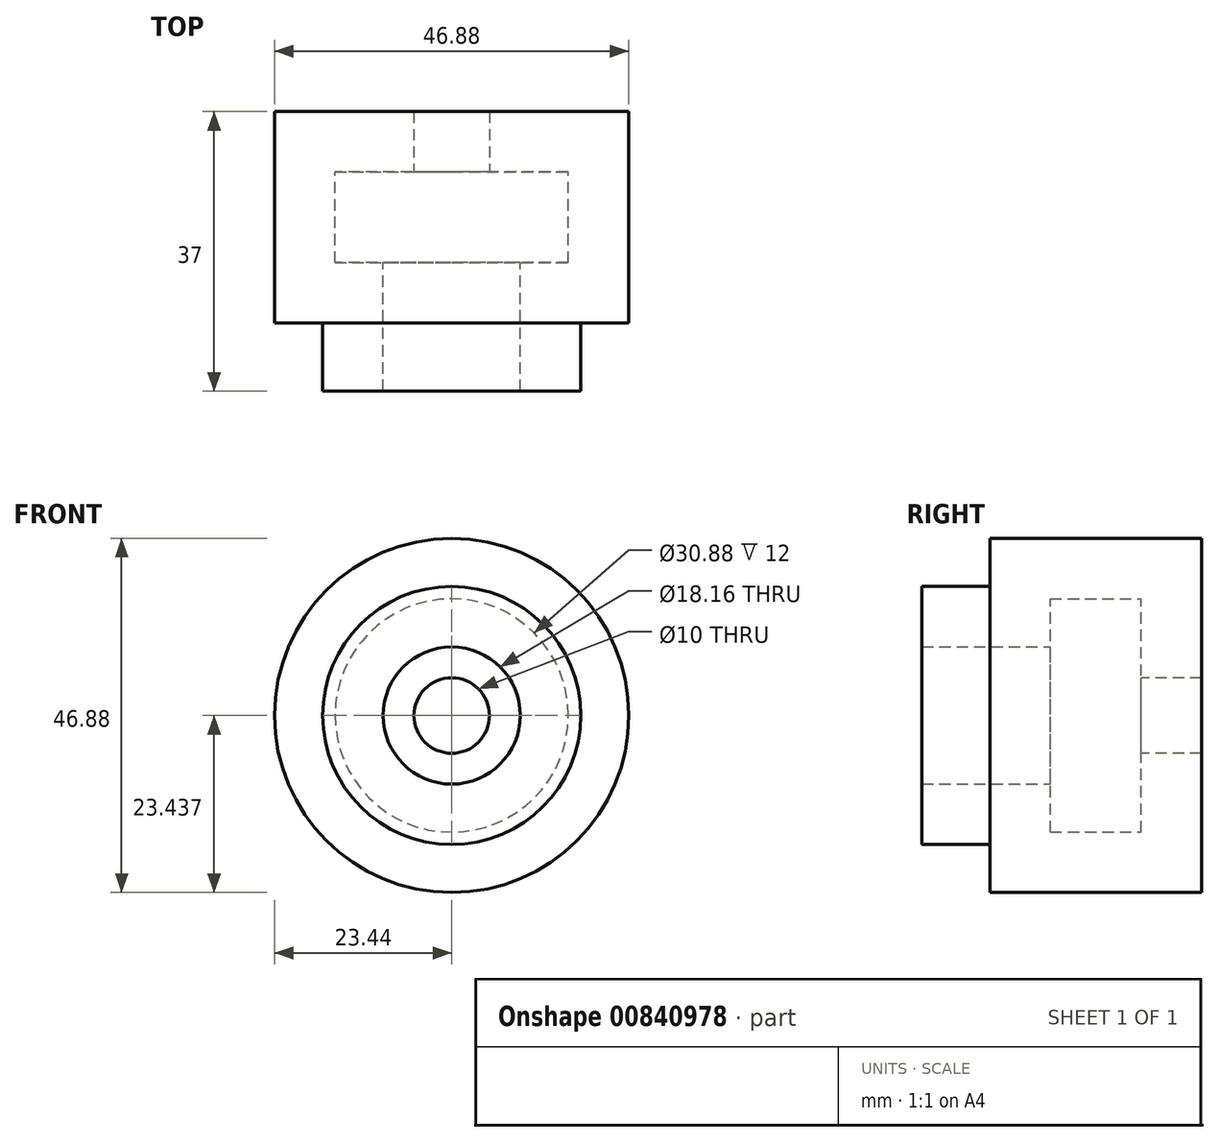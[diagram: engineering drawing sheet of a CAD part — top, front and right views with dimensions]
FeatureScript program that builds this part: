
annotation { "Feature Type Name" : "Feature", "Feature Type Description" : "" }
export const myFeature = defineFeature(function(context is Context, id is Id, definition is map)
    precondition{}
    {
        {
            var Q0;
            Q0=qCreatedBy(makeId("Front.planeOp"),FACE);
            var sketch = newSketch(context, id + "F0", { "sketchPlane" : qUnion([Q0])});
            skCircle(sketch, "E0", {"center": v(0, 23.7) * mm, "radius": 23.44 * mm});
            skSolve(sketch);
        }
        {
            var Q0;
            Q0=makeQuery(id+"F0.imprint","IMPRINT",FACE,{"disambiguationData":[TD([[makeQuery(id+"F0.imprint","IMPRINT",EDGE,{"derivedFrom":sQuery(id+"F0.wireOp",EDGE,"E0")}),1.0]])]});
            var Q1;
            Q1=sQuery(id+"F0.wireOp",EDGE,"E0");
            extrude(context, id + "F1", {"entities" : qUnion([Q0]), "surfaceEntities" : qUnion([Q1]), "depth" : 28 * mm, "offsetDistance" : 25.4 * mm});
        }
        {
            var Q0;
            Q0=makeQuery(id+"F1.opExtrude","SWEPT_BODY",BODY,{"disambiguationData":[OSD([sQuery(id+"F0.wireOp",EDGE,"E0")])]});
            transform(context, id + "F2", {"entities" : qUnion([Q0]), "transformType" : TransformType.TRANSLATION_3D, "dx" : 0 * mm, "dy" : 25.65 * mm, "dz" : 0 * mm, "makeCopy" : false});
        }
        {
            var Q0;
            Q0=makeQuery(id+"F1.opExtrude","CAP_FACE",FACE,{"disambiguationData":[OSD([sQuery(id+"F0.wireOp",EDGE,"E0")])],"isStart":false});
            var sketch = newSketch(context, id + "F3", { "sketchPlane" : qUnion([Q0])});
            skCircle(sketch, "E1", {"center": v(0, 23.7) * mm, "radius": 17.08 * mm});
            skSolve(sketch);
        }
        {
            var Q0;
            Q0=makeQuery(id+"F3.imprint","IMPRINT",FACE,{"disambiguationData":[TD([[makeQuery(id+"F3.imprint","IMPRINT",EDGE,{"derivedFrom":sQuery(id+"F3.wireOp",EDGE,"E1")}),1.0]])]});
            extrude(context, id + "F4", {"entities" : qUnion([Q0]), "operationType" : NewBodyOperationType.ADD, "surfaceOperationType" : NewSurfaceOperationType.ADD, "depth" : 9 * mm, "offsetDistance" : 25 * mm});
        }
        {
            var Q0;
            Q0=makeQuery(id+"F4.opExtrude","CAP_FACE",FACE,{"disambiguationData":[OSD([sQuery(id+"F3.wireOp",EDGE,"E1")])],"isStart":false});
            var Q1;
            Q1=makeQuery(id+"F1.opExtrude","SWEPT_BODY",BODY,{"disambiguationData":[OSD([sQuery(id+"F0.wireOp",EDGE,"E0")])]});
            shell(context, id + "F5", {"entities" : qUnion([Q0]), "parts" : qUnion([Q1]), "thickness" : 8 * mm});
        }
        {
            var Q0;
            Q0=sQuery(id+"F0.wireOp",VERTEX,"E0.center");
            var Q1;
            Q1=makeQuery(id+"F1.opExtrude","SWEPT_BODY",BODY,{"disambiguationData":[OSD([sQuery(id+"F0.wireOp",EDGE,"E0")])]});
            hole(context, id + "F6", {"style" : HoleStyle.SIMPLE, "endStyle" : HoleEndStyle.THROUGH, "holeDiameter" : 10 * mm, "majorDiameter" : 5 * mm, "isTappedThrough" : true, "tappedDepth" : 12 * mm, "tapClearance" : 3, "startFromSketch" : true, "locations" : qUnion([Q0]), "scope" : qUnion([Q1])});
        }
    });
